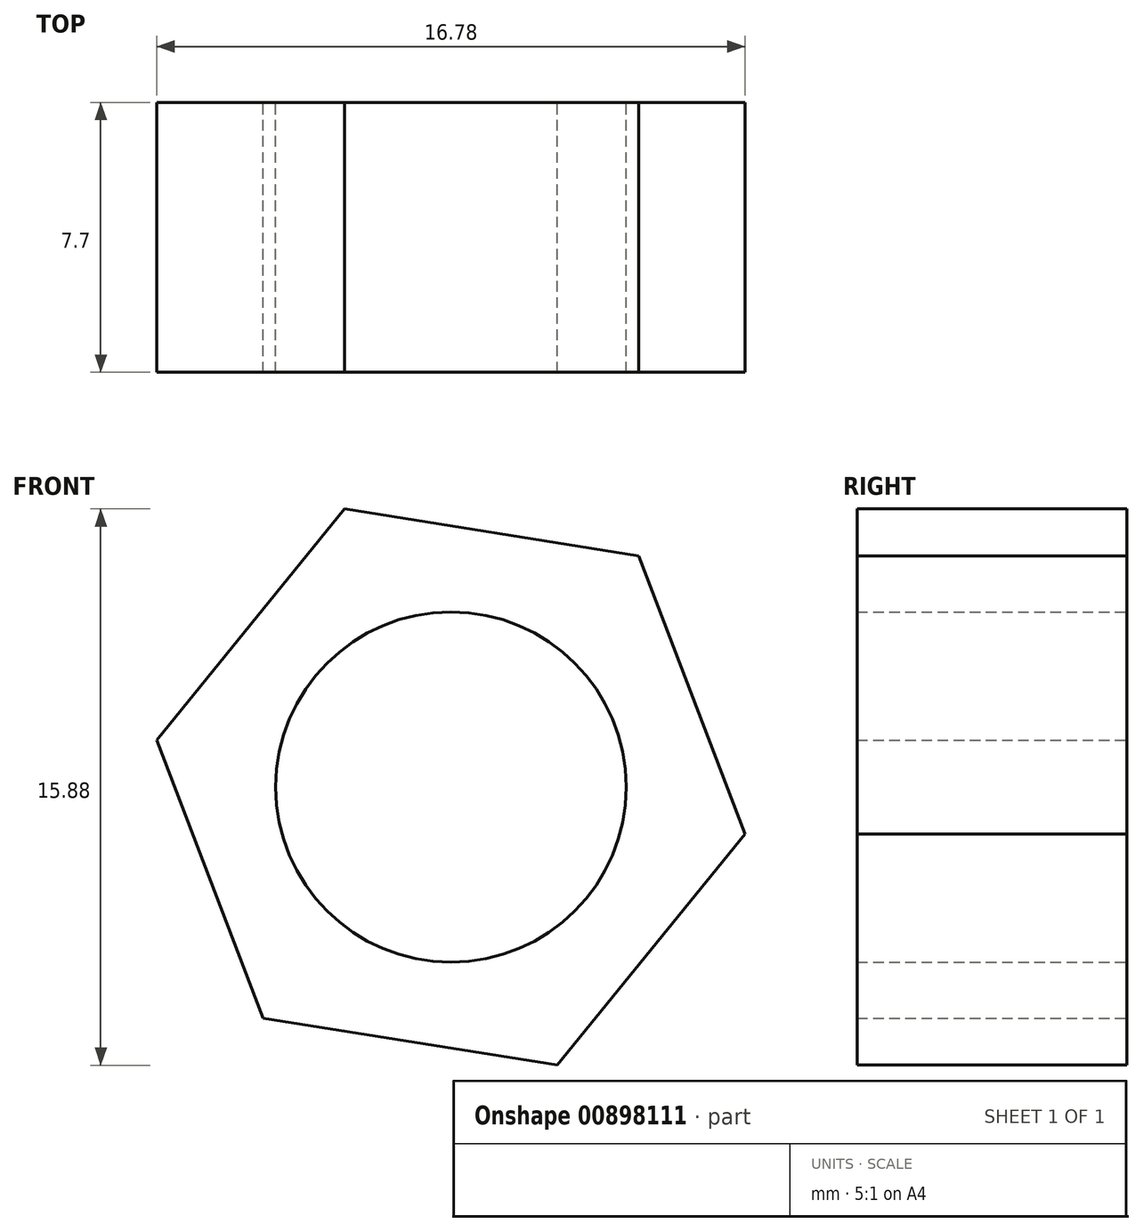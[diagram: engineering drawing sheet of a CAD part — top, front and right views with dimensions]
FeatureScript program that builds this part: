
annotation { "Feature Type Name" : "Feature", "Feature Type Description" : "" }
export const myFeature = defineFeature(function(context is Context, id is Id, definition is map)
    precondition{}
    {
        {
            var Q0;
            Q0=qCreatedBy(makeId("Front.planeOp"),FACE);
            var sketch = newSketch(context, id + "F0", { "sketchPlane" : qUnion([Q0])});
            skCircle(sketch, "E0", {"center": v(0, 0) * mm, "radius": 8.5 * mm});
            skCircle(sketch, "E1.cCircle", {"center": v(0, 0) * mm, "radius": 8.5 * mm, "construction": true});
            skLineSegment(sketch, "E1.0", {"start": v(-8.4, 1.34) * mm, "end": v(-3.04, 7.94) * mm});
            skLineSegment(sketch, "E1.1", {"start": v(-3.04, 7.94) * mm, "end": v(5.36, 6.6) * mm});
            skLineSegment(sketch, "E1.2", {"start": v(5.36, 6.6) * mm, "end": v(8.4, -1.34) * mm});
            skLineSegment(sketch, "E1.3", {"start": v(8.4, -1.34) * mm, "end": v(3.04, -7.94) * mm});
            skLineSegment(sketch, "E1.4", {"start": v(3.04, -7.94) * mm, "end": v(-5.36, -6.6) * mm});
            skLineSegment(sketch, "E1.5", {"start": v(-5.36, -6.6) * mm, "end": v(-8.4, 1.34) * mm});
            skCircle(sketch, "E2", {"center": v(0, 0) * mm, "radius": 5 * mm});
            skSolve(sketch);
        }
        {
            var Q0;
            Q0=makeQuery(id+"F0.imprint","IMPRINT",FACE,{"disambiguationData":[TD([[makeQuery(id+"F0.imprint","IMPRINT",EDGE,{"derivedFrom":sQuery(id+"F0.wireOp",EDGE,"E1.0")}),-1.0]])]});
            extrude(context, id + "F1", {"entities" : qUnion([Q0]), "depth" : 7.7 * mm, "offsetDistance" : 25 * mm});
        }
    });
